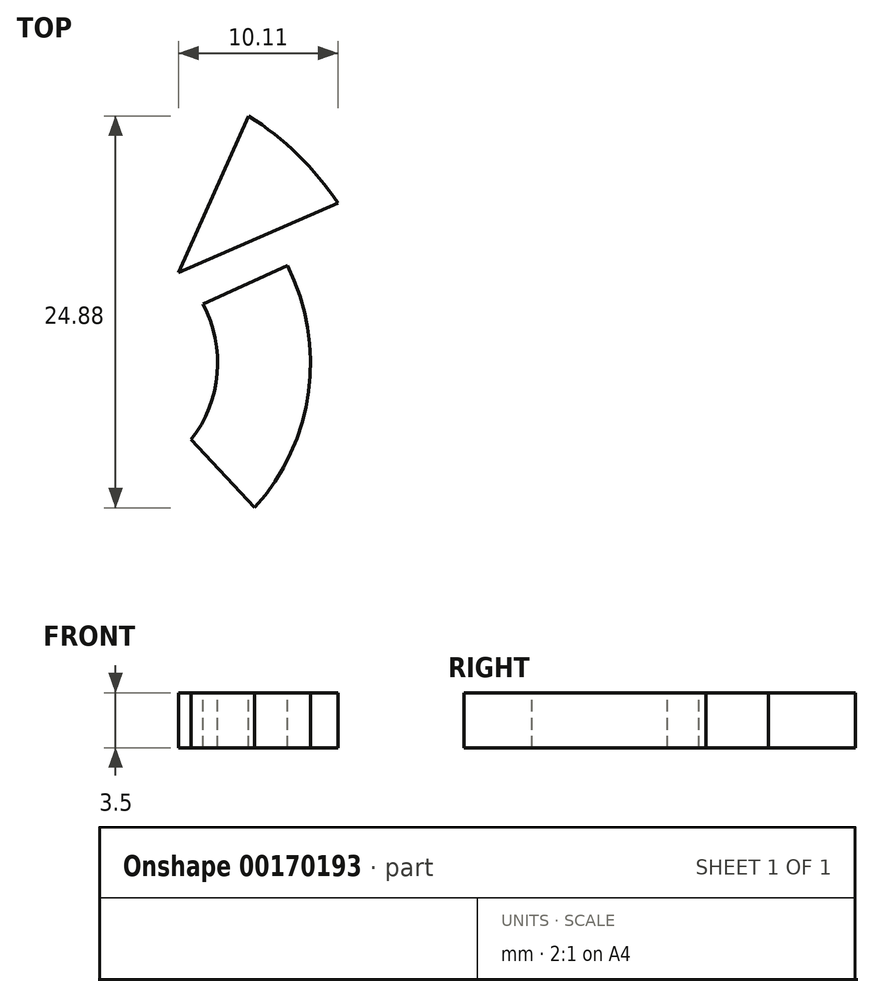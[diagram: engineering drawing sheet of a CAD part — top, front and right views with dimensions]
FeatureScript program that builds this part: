
annotation { "Feature Type Name" : "Feature", "Feature Type Description" : "" }
export const myFeature = defineFeature(function(context is Context, id is Id, definition is map)
    precondition{}
    {
        {
            var Q0;
            Q0=qCreatedBy(makeId("Top.planeOp"),FACE);
            var sketch = newSketch(context, id + "F0", { "sketchPlane" : qUnion([Q0])});
            skLineSegment(sketch, "E0.bottom", {"start": v(-153.76, 79.26) * mm, "end": v(196.24, 79.26) * mm});
            skLineSegment(sketch, "E0.top", {"start": v(-153.76, -13.12) * mm, "end": v(196.24, -13.12) * mm});
            skLineSegment(sketch, "E0.left", {"start": v(-153.76, 79.26) * mm, "end": v(-153.76, -13.12) * mm});
            skLineSegment(sketch, "E0.right", {"start": v(196.24, 79.26) * mm, "end": v(196.24, -13.12) * mm});
            skCircle(sketch, "E1", {"center": v(-123.39, 12.33) * mm, "radius": 17.49 * mm});
            skCircle(sketch, "E2", {"center": v(-123.39, 12.33) * mm, "radius": 11.88 * mm});
            skCircle(sketch, "E3", {"center": v(-123.39, 12.33) * mm, "radius": 9.49 * mm});
            skCircle(sketch, "E4", {"center": v(-123.39, 12.33) * mm, "radius": 3.6 * mm});
            skCircle(sketch, "E5", {"center": v(-123.39, 12.33) * mm, "radius": 7.83 * mm});
            skCircle(sketch, "E6", {"center": v(-123.39, 12.33) * mm, "radius": 13.72 * mm});
            skLineSegment(sketch, "E7", {"start": v(-123.39, 12.33) * mm, "end": v(-116.12, 28.24) * mm});
            skLineSegment(sketch, "E8", {"start": v(-112.54, -1.39) * mm, "end": v(-121.72, 9.15) * mm});
            skCircle(sketch, "E9", {"center": v(-123.39, 12.33) * mm, "radius": 18.48 * mm});
            skLineSegment(sketch, "E10", {"start": v(-118.04, 18.06) * mm, "end": v(-113.59, 28) * mm});
            skLineSegment(sketch, "E11", {"start": v(-118.04, 18.06) * mm, "end": v(-107.93, 22.47) * mm});
            skLineSegment(sketch, "E12", {"start": v(-116.5, 16.06) * mm, "end": v(-111.14, 18.51) * mm});
            skLineSegment(sketch, "E13", {"start": v(-117.25, 7.47) * mm, "end": v(-113.21, 3.13) * mm});
            skText(sketch, "E14", { "text": "Ecoles Supérieures", "fontName": "OpenSans-Regular.ttf"});
            skText(sketch, "E15", { "text": "CCI PORTES DE NORMANDIE", "fontName": "OpenSans-Regular.ttf"});
            const initialGuessF0  = {"E14": [-0.14265, 0.03824, 1, 0, 0.02692], "E15": [-0.10308, 0.00715, 1, 0, 0.01356]};
            skSetInitialGuess(sketch, initialGuessF0);
            skSolve(sketch);
        }
        {
            var Q0;
            Q0=makeQuery(id+"F0.imprint","IMPRINT",FACE,{"disambiguationData":[TD([[makeQuery(id+"F0.imprint","IMPRINT",EDGE,{"derivedFrom":sQuery(id+"F0.wireOp",EDGE,"E14.sketch_text.stroke-0")}),-1.0]])]});
            var Q1;
            Q1=makeQuery(id+"F0.imprint","IMPRINT",FACE,{"disambiguationData":[TD([[makeQuery(id+"F0.imprint","IMPRINT",EDGE,{"derivedFrom":sQuery(id+"F0.wireOp",EDGE,"E14.sketch_text.stroke-12")}),-1.0]])]});
            var Q2;
            Q2=makeQuery(id+"F0.imprint","IMPRINT",FACE,{"disambiguationData":[TD([[makeQuery(id+"F0.imprint","IMPRINT",EDGE,{"derivedFrom":sQuery(id+"F0.wireOp",EDGE,"E14.sketch_text.stroke-27")}),-1.0]])]});
            var Q3;
            Q3=makeQuery(id+"F0.imprint","IMPRINT",FACE,{"disambiguationData":[TD([[makeQuery(id+"F0.imprint","IMPRINT",EDGE,{"derivedFrom":sQuery(id+"F0.wireOp",EDGE,"E14.sketch_text.stroke-44")}),-1.0]])]});
            var Q4;
            Q4=makeQuery(id+"F0.imprint","IMPRINT",FACE,{"disambiguationData":[TD([[makeQuery(id+"F0.imprint","IMPRINT",EDGE,{"derivedFrom":sQuery(id+"F0.wireOp",EDGE,"E14.sketch_text.stroke-48")}),-1.0]])]});
            var Q5;
            Q5=makeQuery(id+"F0.imprint","IMPRINT",FACE,{"disambiguationData":[TD([[makeQuery(id+"F0.imprint","IMPRINT",EDGE,{"derivedFrom":sQuery(id+"F0.wireOp",EDGE,"E14.sketch_text.stroke-67")}),-1.0]])]});
            var Q6;
            Q6=makeQuery(id+"F0.imprint","IMPRINT",FACE,{"disambiguationData":[TD([[makeQuery(id+"F0.imprint","IMPRINT",EDGE,{"derivedFrom":sQuery(id+"F0.wireOp",EDGE,"E14.sketch_text.stroke-92")}),-1.0]])]});
            var Q7;
            Q7=makeQuery(id+"F0.imprint","IMPRINT",FACE,{"disambiguationData":[TD([[makeQuery(id+"F0.imprint","IMPRINT",EDGE,{"derivedFrom":sQuery(id+"F0.wireOp",EDGE,"E14.sketch_text.stroke-117")}),-1.0]])]});
            var Q8;
            Q8=makeQuery(id+"F0.imprint","IMPRINT",FACE,{"disambiguationData":[TD([[makeQuery(id+"F0.imprint","IMPRINT",EDGE,{"derivedFrom":sQuery(id+"F0.wireOp",EDGE,"E14.sketch_text.stroke-134")}),-1.0]])]});
            var Q9;
            Q9=makeQuery(id+"F0.imprint","IMPRINT",FACE,{"disambiguationData":[TD([[makeQuery(id+"F0.imprint","IMPRINT",EDGE,{"derivedFrom":sQuery(id+"F0.wireOp",EDGE,"E15.sketch_text.stroke-34")}),-1.0]])]});
            var Q10;
            Q10=makeQuery(id+"F0.imprint","IMPRINT",FACE,{"disambiguationData":[TD([[makeQuery(id+"F0.imprint","IMPRINT",EDGE,{"derivedFrom":sQuery(id+"F0.wireOp",EDGE,"E15.sketch_text.stroke-49")}),-1.0]])]});
            var Q11;
            Q11=makeQuery(id+"F0.imprint","IMPRINT",FACE,{"disambiguationData":[TD([[makeQuery(id+"F0.imprint","IMPRINT",EDGE,{"derivedFrom":sQuery(id+"F0.wireOp",EDGE,"E15.sketch_text.stroke-65")}),-1.0]])]});
            var Q12;
            Q12=makeQuery(id+"F0.imprint","IMPRINT",FACE,{"disambiguationData":[TD([[makeQuery(id+"F0.imprint","IMPRINT",EDGE,{"derivedFrom":sQuery(id+"F0.wireOp",EDGE,"E15.sketch_text.stroke-83")}),-1.0]])]});
            var Q13;
            Q13=makeQuery(id+"F0.imprint","IMPRINT",FACE,{"disambiguationData":[TD([[makeQuery(id+"F0.imprint","IMPRINT",EDGE,{"derivedFrom":sQuery(id+"F0.wireOp",EDGE,"E15.sketch_text.stroke-91")}),-1.0]])]});
            var Q14;
            Q14=makeQuery(id+"F0.imprint","IMPRINT",FACE,{"disambiguationData":[TD([[makeQuery(id+"F0.imprint","IMPRINT",EDGE,{"derivedFrom":sQuery(id+"F0.wireOp",EDGE,"E15.sketch_text.stroke-0")}),-1.0]])]});
            var Q15;
            Q15=makeQuery(id+"F0.imprint","IMPRINT",FACE,{"disambiguationData":[TD([[makeQuery(id+"F0.imprint","IMPRINT",EDGE,{"derivedFrom":sQuery(id+"F0.wireOp",EDGE,"E15.sketch_text.stroke-15")}),-1.0]])]});
            var Q16;
            Q16=makeQuery(id+"F0.imprint","IMPRINT",FACE,{"disambiguationData":[TD([[makeQuery(id+"F0.imprint","IMPRINT",EDGE,{"derivedFrom":sQuery(id+"F0.wireOp",EDGE,"E15.sketch_text.stroke-30")}),-1.0]])]});
            var Q17;
            Q17=makeQuery(id+"F0.imprint","IMPRINT",FACE,{"disambiguationData":[TD([[makeQuery(id+"F0.imprint","IMPRINT",EDGE,{"derivedFrom":sQuery(id+"F0.wireOp",EDGE,"E14.sketch_text.stroke-159")}),-1.0]])]});
            var Q18;
            Q18=makeQuery(id+"F0.imprint","IMPRINT",FACE,{"disambiguationData":[TD([[makeQuery(id+"F0.imprint","IMPRINT",EDGE,{"derivedFrom":sQuery(id+"F0.wireOp",EDGE,"E14.sketch_text.stroke-178")}),-1.0]])]});
            var Q19;
            Q19=makeQuery(id+"F0.imprint","IMPRINT",FACE,{"disambiguationData":[TD([[makeQuery(id+"F0.imprint","IMPRINT",EDGE,{"derivedFrom":sQuery(id+"F0.wireOp",EDGE,"E14.sketch_text.stroke-186")}),-1.0]])]});
            var Q20;
            Q20=makeQuery(id+"F0.imprint","IMPRINT",FACE,{"disambiguationData":[TD([[makeQuery(id+"F0.imprint","IMPRINT",EDGE,{"derivedFrom":sQuery(id+"F0.wireOp",EDGE,"E14.sketch_text.stroke-230")}),-1.0]])]});
            var Q21;
            Q21=makeQuery(id+"F0.imprint","IMPRINT",FACE,{"disambiguationData":[TD([[makeQuery(id+"F0.imprint","IMPRINT",EDGE,{"derivedFrom":sQuery(id+"F0.wireOp",EDGE,"E14.sketch_text.stroke-247")}),-1.0]])]});
            var Q22;
            Q22=makeQuery(id+"F0.imprint","IMPRINT",FACE,{"disambiguationData":[TD([[makeQuery(id+"F0.imprint","IMPRINT",EDGE,{"derivedFrom":sQuery(id+"F0.wireOp",EDGE,"E14.sketch_text.stroke-279")}),-1.0]])]});
            var Q23;
            Q23=makeQuery(id+"F0.imprint","IMPRINT",FACE,{"disambiguationData":[TD([[makeQuery(id+"F0.imprint","IMPRINT",EDGE,{"derivedFrom":sQuery(id+"F0.wireOp",EDGE,"E14.sketch_text.stroke-260")}),-1.0]])]});
            var Q24;
            Q24=makeQuery(id+"F0.imprint","IMPRINT",FACE,{"disambiguationData":[TD([[makeQuery(id+"F0.imprint","IMPRINT",EDGE,{"derivedFrom":sQuery(id+"F0.wireOp",EDGE,"E14.sketch_text.stroke-211")}),-1.0]])]});
            var Q25;
            Q25=makeQuery(id+"F0.imprint","IMPRINT",FACE,{"disambiguationData":[TD([[makeQuery(id+"F0.imprint","IMPRINT",EDGE,{"derivedFrom":sQuery(id+"F0.wireOp",EDGE,"E14.sketch_text.stroke-199")}),-1.0]])]});
            var Q26;
            Q26=makeQuery(id+"F0.imprint","IMPRINT",FACE,{"disambiguationData":[TD([[makeQuery(id+"F0.imprint","IMPRINT",EDGE,{"derivedFrom":sQuery(id+"F0.wireOp",EDGE,"E14.sketch_text.stroke-203")}),-1.0]])]});
            var Q27;
            Q27=makeQuery(id+"F0.imprint","IMPRINT",FACE,{"disambiguationData":[TD([[makeQuery(id+"F0.imprint","IMPRINT",EDGE,{"derivedFrom":sQuery(id+"F0.wireOp",EDGE,"E15.sketch_text.stroke-263")}),-1.0]])]});
            var Q28;
            Q28=makeQuery(id+"F0.imprint","IMPRINT",FACE,{"disambiguationData":[TD([[makeQuery(id+"F0.imprint","IMPRINT",EDGE,{"derivedFrom":sQuery(id+"F0.wireOp",EDGE,"E15.sketch_text.stroke-267")}),-1.0]])]});
            var Q29;
            Q29=makeQuery(id+"F0.imprint","IMPRINT",FACE,{"disambiguationData":[TD([[makeQuery(id+"F0.imprint","IMPRINT",EDGE,{"derivedFrom":sQuery(id+"F0.wireOp",EDGE,"E15.sketch_text.stroke-249")}),-1.0]])]});
            var Q30;
            Q30=makeQuery(id+"F0.imprint","IMPRINT",FACE,{"disambiguationData":[TD([[makeQuery(id+"F0.imprint","IMPRINT",EDGE,{"derivedFrom":sQuery(id+"F0.wireOp",EDGE,"E15.sketch_text.stroke-103")}),-1.0]])]});
            var Q31;
            Q31=makeQuery(id+"F0.imprint","IMPRINT",FACE,{"disambiguationData":[TD([[makeQuery(id+"F0.imprint","IMPRINT",EDGE,{"derivedFrom":sQuery(id+"F0.wireOp",EDGE,"E15.sketch_text.stroke-128")}),-1.0]])]});
            var Q32;
            Q32=makeQuery(id+"F0.imprint","IMPRINT",FACE,{"disambiguationData":[TD([[makeQuery(id+"F0.imprint","IMPRINT",EDGE,{"derivedFrom":sQuery(id+"F0.wireOp",EDGE,"E15.sketch_text.stroke-154")}),-1.0]])]});
            var Q33;
            Q33=makeQuery(id+"F0.imprint","IMPRINT",FACE,{"disambiguationData":[TD([[makeQuery(id+"F0.imprint","IMPRINT",EDGE,{"derivedFrom":sQuery(id+"F0.wireOp",EDGE,"E15.sketch_text.stroke-142")}),-1.0]])]});
            var Q34;
            Q34=makeQuery(id+"F0.imprint","IMPRINT",FACE,{"disambiguationData":[TD([[makeQuery(id+"F0.imprint","IMPRINT",EDGE,{"derivedFrom":sQuery(id+"F0.wireOp",EDGE,"E15.sketch_text.stroke-169")}),-1.0]])]});
            var Q35;
            Q35=makeQuery(id+"F0.imprint","IMPRINT",FACE,{"disambiguationData":[TD([[makeQuery(id+"F0.imprint","IMPRINT",EDGE,{"derivedFrom":sQuery(id+"F0.wireOp",EDGE,"E15.sketch_text.stroke-185")}),-1.0]])]});
            var Q36;
            Q36=makeQuery(id+"F0.imprint","IMPRINT",FACE,{"disambiguationData":[TD([[makeQuery(id+"F0.imprint","IMPRINT",EDGE,{"derivedFrom":sQuery(id+"F0.wireOp",EDGE,"E15.sketch_text.stroke-203")}),-1.0]])]});
            var Q37;
            Q37=makeQuery(id+"F0.imprint","IMPRINT",FACE,{"disambiguationData":[TD([[makeQuery(id+"F0.imprint","IMPRINT",EDGE,{"derivedFrom":sQuery(id+"F0.wireOp",EDGE,"E15.sketch_text.stroke-234")}),-1.0]])]});
            var Q38;
            Q38=makeQuery(id+"F0.imprint","IMPRINT",FACE,{"disambiguationData":[TD([[makeQuery(id+"F0.imprint","IMPRINT",EDGE,{"derivedFrom":sQuery(id+"F0.wireOp",EDGE,"E15.sketch_text.stroke-221")}),-1.0]])]});
            var Q39;
            {var subQ0=sQuery(id+"F0.wireOp",EDGE,"E8");var subQ1=sQuery(id+"F0.wireOp",EDGE,"E4");var subQ2=makeQuery(id+"F0.imprint","INTERSECT",VERTEX,{"derivedFrom":[subQ1,subQ0]});Q39=makeQuery(id+"F0.imprint","IMPRINT",FACE,{"disambiguationData":[TD([[makeQuery(id+"F0.imprint","IMPRINT",EDGE,{"disambiguationData":[TD([[subQ2,1.0]])],"derivedFrom":subQ1}),-1.0]])]});}
            var Q40;
            {var subQ0=sQuery(id+"F0.wireOp",EDGE,"E7");var subQ1=sQuery(id+"F0.wireOp",EDGE,"E3");var subQ2=makeQuery(id+"F0.imprint","INTERSECT",VERTEX,{"derivedFrom":[subQ1,subQ0]});Q40=makeQuery(id+"F0.imprint","IMPRINT",FACE,{"disambiguationData":[TD([[makeQuery(id+"F0.imprint","IMPRINT",EDGE,{"disambiguationData":[TD([[subQ2,-1.0]])],"derivedFrom":subQ1}),1.0]])]});}
            var Q41;
            {var subQ0=sQuery(id+"F0.wireOp",EDGE,"E7");var subQ1=sQuery(id+"F0.wireOp",EDGE,"E2");var subQ2=makeQuery(id+"F0.imprint","INTERSECT",VERTEX,{"derivedFrom":[subQ1,subQ0]});Q41=makeQuery(id+"F0.imprint","IMPRINT",FACE,{"disambiguationData":[TD([[makeQuery(id+"F0.imprint","IMPRINT",EDGE,{"disambiguationData":[TD([[subQ2,-1.0]])],"derivedFrom":subQ1}),-1.0]])]});}
            var Q42;
            {var subQ0=sQuery(id+"F0.wireOp",EDGE,"E7");var subQ1=sQuery(id+"F0.wireOp",EDGE,"E1");var subQ2=makeQuery(id+"F0.imprint","INTERSECT",VERTEX,{"derivedFrom":[subQ1,subQ0]});Q42=makeQuery(id+"F0.imprint","IMPRINT",FACE,{"disambiguationData":[TD([[makeQuery(id+"F0.imprint","IMPRINT",EDGE,{"disambiguationData":[TD([[subQ2,-1.0]])],"derivedFrom":subQ1}),1.0]])]});}
            extrude(context, id + "F1", {"entities" : qUnion([Q0, Q1, Q2, Q3, Q4, Q5, Q6, Q7, Q8, Q9, Q10, Q11, Q12, Q13, Q14, Q15, Q16, Q17, Q18, Q19, Q20, Q21, Q22, Q23, Q24, Q25, Q26, Q27, Q28, Q29, Q30, Q31, Q32, Q33, Q34, Q35, Q36, Q37, Q38, Q39, Q40, Q41, Q42]), "depth" : 1.5 * mm});
        }
        {
            var Q0;
            Q0=makeQuery(id+"F0.imprint","IMPRINT",FACE,{"disambiguationData":[TD([[makeQuery(id+"F0.imprint","IMPRINT",EDGE,{"derivedFrom":sQuery(id+"F0.wireOp",EDGE,"E0.bottom")}),-1.0]])]});
            var sketch = newSketch(context, id + "F2", { "sketchPlane" : qUnion([Q0])});
            skLineSegment(sketch, "E16.bottom", {"start": v(-154.27, -13.4) * mm, "end": v(196.36, -13.4) * mm});
            skLineSegment(sketch, "E16.top", {"start": v(-154.27, 78.37) * mm, "end": v(196.36, 78.37) * mm});
            skLineSegment(sketch, "E16.left", {"start": v(-154.27, -13.4) * mm, "end": v(-154.27, 78.37) * mm});
            skLineSegment(sketch, "E16.right", {"start": v(196.36, -13.4) * mm, "end": v(196.36, 78.37) * mm});
            skSolve(sketch);
        }
        {
            var Q0;
            Q0=qSketchRegion(id+"F2",true);
            var Q1;
            {var subQ5=makeQuery(id+"F0.imprint","IMPRINT",EDGE,{"derivedFrom":sQuery(id+"F0.wireOp",EDGE,"E0.top")});Q1=makeQuery(id+"F2.imprint","IMPRINT",FACE,{"disambiguationData":[TD([[makeQuery(id+"F2.imprint","IMPRINT",EDGE,{"derivedFrom":subQ5}),1.0]])]});}
            extrude(context, id + "F3", {"entities" : qUnion([Q0, Q1]), "oppositeDirection" : true, "depth" : 2.7 * mm});
        }
        {
            var Q0;
            Q0=makeQuery(id+"F3.opExtrude","SWEPT_EDGE",EDGE,{"disambiguationData":[OSD([sQuery(id+"F2.wireOp",EDGE,"E16.bottom"),sQuery(id+"F2.wireOp",EDGE,"E16.right")])]});
            var Q1;
            Q1=makeQuery(id+"F3.opExtrude","SWEPT_EDGE",EDGE,{"disambiguationData":[OSD([sQuery(id+"F2.wireOp",EDGE,"E16.top"),sQuery(id+"F2.wireOp",EDGE,"E16.right")])]});
            var Q2;
            Q2=makeQuery(id+"F3.opExtrude","SWEPT_EDGE",EDGE,{"disambiguationData":[OSD([sQuery(id+"F2.wireOp",EDGE,"E16.bottom"),sQuery(id+"F2.wireOp",EDGE,"E16.left")])]});
            var Q3;
            Q3=makeQuery(id+"F3.opExtrude","SWEPT_EDGE",EDGE,{"disambiguationData":[OSD([sQuery(id+"F2.wireOp",EDGE,"E16.top"),sQuery(id+"F2.wireOp",EDGE,"E16.left")])]});
            fillet(context, id + "F4", {"entities" : qUnion([Q0, Q1, Q2, Q3]), "radius" : 10 * mm, "tangentPropagation" : true, "allowEdgeOverflow" : false});
        }
        {
            var Q0;
            {var subQ0=sQuery(id+"F0.wireOp",EDGE,"E12");var subQ1=sQuery(id+"F0.wireOp",EDGE,"E3");var subQ2=makeQuery(id+"F0.imprint","INTERSECT",VERTEX,{"derivedFrom":[subQ1,subQ0]});Q0=makeQuery(id+"F0.imprint","IMPRINT",FACE,{"disambiguationData":[TD([[makeQuery(id+"F0.imprint","IMPRINT",EDGE,{"disambiguationData":[TD([[subQ2,1.0]])],"derivedFrom":subQ1}),1.0]])]});}
            var Q1;
            {var subQ0=sQuery(id+"F0.wireOp",EDGE,"E12");var subQ1=sQuery(id+"F0.wireOp",EDGE,"E2");var subQ2=makeQuery(id+"F0.imprint","INTERSECT",VERTEX,{"derivedFrom":[subQ1,subQ0]});Q1=makeQuery(id+"F0.imprint","IMPRINT",FACE,{"disambiguationData":[TD([[makeQuery(id+"F0.imprint","IMPRINT",EDGE,{"disambiguationData":[TD([[subQ2,1.0]])],"derivedFrom":subQ1}),1.0]])]});}
            var Q2;
            {var subQ0=sQuery(id+"F0.wireOp",EDGE,"E12");var subQ1=sQuery(id+"F0.wireOp",EDGE,"E2");var subQ2=makeQuery(id+"F0.imprint","INTERSECT",VERTEX,{"derivedFrom":[subQ1,subQ0]});Q2=makeQuery(id+"F0.imprint","IMPRINT",FACE,{"disambiguationData":[TD([[makeQuery(id+"F0.imprint","IMPRINT",EDGE,{"disambiguationData":[TD([[subQ2,1.0]])],"derivedFrom":subQ1}),-1.0]])]});}
            var Q3;
            {var subQ0=sQuery(id+"F0.wireOp",EDGE,"E11");var subQ1=sQuery(id+"F0.wireOp",EDGE,"E3");var subQ2=makeQuery(id+"F0.imprint","INTERSECT",VERTEX,{"derivedFrom":[subQ1,subQ0]});Q3=makeQuery(id+"F0.imprint","IMPRINT",FACE,{"disambiguationData":[TD([[makeQuery(id+"F0.imprint","IMPRINT",EDGE,{"disambiguationData":[TD([[subQ2,-1.0]])],"derivedFrom":subQ1}),1.0]])]});}
            var Q4;
            {var subQ0=sQuery(id+"F0.wireOp",EDGE,"E11");var subQ1=sQuery(id+"F0.wireOp",EDGE,"E2");var subQ2=makeQuery(id+"F0.imprint","INTERSECT",VERTEX,{"derivedFrom":[subQ1,subQ0]});Q4=makeQuery(id+"F0.imprint","IMPRINT",FACE,{"disambiguationData":[TD([[makeQuery(id+"F0.imprint","IMPRINT",EDGE,{"disambiguationData":[TD([[subQ2,-1.0]])],"derivedFrom":subQ1}),1.0]])]});}
            var Q5;
            {var subQ0=sQuery(id+"F0.wireOp",EDGE,"E10");var subQ1=sQuery(id+"F0.wireOp",EDGE,"E1");var subQ2=makeQuery(id+"F0.imprint","INTERSECT",VERTEX,{"derivedFrom":[subQ1,subQ0]});Q5=makeQuery(id+"F0.imprint","IMPRINT",FACE,{"disambiguationData":[TD([[makeQuery(id+"F0.imprint","IMPRINT",EDGE,{"disambiguationData":[TD([[subQ2,1.0]])],"derivedFrom":subQ1}),1.0]])]});}
            var Q6;
            {var subQ0=sQuery(id+"F0.wireOp",EDGE,"E10");var subQ1=sQuery(id+"F0.wireOp",EDGE,"E1");var subQ2=makeQuery(id+"F0.imprint","INTERSECT",VERTEX,{"derivedFrom":[subQ1,subQ0]});Q6=makeQuery(id+"F0.imprint","IMPRINT",FACE,{"disambiguationData":[TD([[makeQuery(id+"F0.imprint","IMPRINT",EDGE,{"disambiguationData":[TD([[subQ2,1.0]])],"derivedFrom":subQ1}),-1.0]])]});}
            var Q7;
            {var subQ0=sQuery(id+"F0.wireOp",EDGE,"E11");var subQ1=sQuery(id+"F0.wireOp",EDGE,"E2");var subQ2=makeQuery(id+"F0.imprint","INTERSECT",VERTEX,{"derivedFrom":[subQ1,subQ0]});Q7=makeQuery(id+"F0.imprint","IMPRINT",FACE,{"disambiguationData":[TD([[makeQuery(id+"F0.imprint","IMPRINT",EDGE,{"disambiguationData":[TD([[subQ2,-1.0]])],"derivedFrom":subQ1}),-1.0]])]});}
            extrude(context, id + "F5", {"entities" : qUnion([Q0, Q1, Q2, Q3, Q4, Q5, Q6, Q7]), "oppositeDirection" : true, "depth" : 2 * mm, "hasSecondDirection" : true, "secondDirectionOppositeDirection" : false, "secondDirectionDepth" : 1.5 * mm});
        }
        {
            var Q0;
            Q0=makeQuery(id+"F1.opExtrude","SWEPT_BODY",BODY,{"disambiguationData":[OSD([sQuery(id+"F0.wireOp",EDGE,"E1"),sQuery(id+"F0.wireOp",EDGE,"E2"),sQuery(id+"F0.wireOp",EDGE,"E7"),sQuery(id+"F0.wireOp",EDGE,"E8")])]});
            var Q1;
            Q1=makeQuery(id+"F1.opExtrude","SWEPT_BODY",BODY,{"disambiguationData":[OSD([sQuery(id+"F0.wireOp",EDGE,"E3"),sQuery(id+"F0.wireOp",EDGE,"E4"),sQuery(id+"F0.wireOp",EDGE,"E7"),sQuery(id+"F0.wireOp",EDGE,"E8")])]});
            var Q2;
            Q2=makeQuery(id+"F1.opExtrude","SWEPT_BODY",BODY,{"disambiguationData":[OSD([sQuery(id+"F0.wireOp",EDGE,"E14.sketch_text.stroke-0"),sQuery(id+"F0.wireOp",EDGE,"E14.sketch_text.stroke-1"),sQuery(id+"F0.wireOp",EDGE,"E14.sketch_text.stroke-2"),sQuery(id+"F0.wireOp",EDGE,"E14.sketch_text.stroke-3"),sQuery(id+"F0.wireOp",EDGE,"E14.sketch_text.stroke-4"),sQuery(id+"F0.wireOp",EDGE,"E14.sketch_text.stroke-5"),sQuery(id+"F0.wireOp",EDGE,"E14.sketch_text.stroke-6"),sQuery(id+"F0.wireOp",EDGE,"E14.sketch_text.stroke-7"),sQuery(id+"F0.wireOp",EDGE,"E14.sketch_text.stroke-8"),sQuery(id+"F0.wireOp",EDGE,"E14.sketch_text.stroke-9"),sQuery(id+"F0.wireOp",EDGE,"E14.sketch_text.stroke-10"),sQuery(id+"F0.wireOp",EDGE,"E14.sketch_text.stroke-11")])]});
            var Q3;
            Q3=makeQuery(id+"F1.opExtrude","SWEPT_BODY",BODY,{"disambiguationData":[OSD([sQuery(id+"F0.wireOp",EDGE,"E14.sketch_text.stroke-12"),sQuery(id+"F0.wireOp",EDGE,"E14.sketch_text.stroke-13"),sQuery(id+"F0.wireOp",EDGE,"E14.sketch_text.stroke-14"),sQuery(id+"F0.wireOp",EDGE,"E14.sketch_text.stroke-15"),sQuery(id+"F0.wireOp",EDGE,"E14.sketch_text.stroke-16"),sQuery(id+"F0.wireOp",EDGE,"E14.sketch_text.stroke-17"),sQuery(id+"F0.wireOp",EDGE,"E14.sketch_text.stroke-18"),sQuery(id+"F0.wireOp",EDGE,"E14.sketch_text.stroke-19"),sQuery(id+"F0.wireOp",EDGE,"E14.sketch_text.stroke-20"),sQuery(id+"F0.wireOp",EDGE,"E14.sketch_text.stroke-21"),sQuery(id+"F0.wireOp",EDGE,"E14.sketch_text.stroke-22"),sQuery(id+"F0.wireOp",EDGE,"E14.sketch_text.stroke-23"),sQuery(id+"F0.wireOp",EDGE,"E14.sketch_text.stroke-24"),sQuery(id+"F0.wireOp",EDGE,"E14.sketch_text.stroke-25"),sQuery(id+"F0.wireOp",EDGE,"E14.sketch_text.stroke-26")])]});
            var Q4;
            Q4=makeQuery(id+"F1.opExtrude","SWEPT_BODY",BODY,{"disambiguationData":[OSD([sQuery(id+"F0.wireOp",EDGE,"E14.sketch_text.stroke-27"),sQuery(id+"F0.wireOp",EDGE,"E14.sketch_text.stroke-28"),sQuery(id+"F0.wireOp",EDGE,"E14.sketch_text.stroke-29"),sQuery(id+"F0.wireOp",EDGE,"E14.sketch_text.stroke-30"),sQuery(id+"F0.wireOp",EDGE,"E14.sketch_text.stroke-31"),sQuery(id+"F0.wireOp",EDGE,"E14.sketch_text.stroke-32"),sQuery(id+"F0.wireOp",EDGE,"E14.sketch_text.stroke-33"),sQuery(id+"F0.wireOp",EDGE,"E14.sketch_text.stroke-34"),sQuery(id+"F0.wireOp",EDGE,"E14.sketch_text.stroke-35"),sQuery(id+"F0.wireOp",EDGE,"E14.sketch_text.stroke-36"),sQuery(id+"F0.wireOp",EDGE,"E14.sketch_text.stroke-37"),sQuery(id+"F0.wireOp",EDGE,"E14.sketch_text.stroke-38"),sQuery(id+"F0.wireOp",EDGE,"E14.sketch_text.stroke-39"),sQuery(id+"F0.wireOp",EDGE,"E14.sketch_text.stroke-40"),sQuery(id+"F0.wireOp",EDGE,"E14.sketch_text.stroke-41"),sQuery(id+"F0.wireOp",EDGE,"E14.sketch_text.stroke-42"),sQuery(id+"F0.wireOp",EDGE,"E14.sketch_text.stroke-43")])]});
            var Q5;
            Q5=makeQuery(id+"F1.opExtrude","SWEPT_BODY",BODY,{"disambiguationData":[OSD([sQuery(id+"F0.wireOp",EDGE,"E14.sketch_text.stroke-44"),sQuery(id+"F0.wireOp",EDGE,"E14.sketch_text.stroke-45"),sQuery(id+"F0.wireOp",EDGE,"E14.sketch_text.stroke-46"),sQuery(id+"F0.wireOp",EDGE,"E14.sketch_text.stroke-47")])]});
            var Q6;
            Q6=makeQuery(id+"F1.opExtrude","SWEPT_BODY",BODY,{"disambiguationData":[OSD([sQuery(id+"F0.wireOp",EDGE,"E14.sketch_text.stroke-48"),sQuery(id+"F0.wireOp",EDGE,"E14.sketch_text.stroke-49"),sQuery(id+"F0.wireOp",EDGE,"E14.sketch_text.stroke-50"),sQuery(id+"F0.wireOp",EDGE,"E14.sketch_text.stroke-51"),sQuery(id+"F0.wireOp",EDGE,"E14.sketch_text.stroke-52"),sQuery(id+"F0.wireOp",EDGE,"E14.sketch_text.stroke-53"),sQuery(id+"F0.wireOp",EDGE,"E14.sketch_text.stroke-54"),sQuery(id+"F0.wireOp",EDGE,"E14.sketch_text.stroke-55"),sQuery(id+"F0.wireOp",EDGE,"E14.sketch_text.stroke-56"),sQuery(id+"F0.wireOp",EDGE,"E14.sketch_text.stroke-57"),sQuery(id+"F0.wireOp",EDGE,"E14.sketch_text.stroke-58"),sQuery(id+"F0.wireOp",EDGE,"E14.sketch_text.stroke-59"),sQuery(id+"F0.wireOp",EDGE,"E14.sketch_text.stroke-60"),sQuery(id+"F0.wireOp",EDGE,"E14.sketch_text.stroke-61"),sQuery(id+"F0.wireOp",EDGE,"E14.sketch_text.stroke-62"),sQuery(id+"F0.wireOp",EDGE,"E14.sketch_text.stroke-63"),sQuery(id+"F0.wireOp",EDGE,"E14.sketch_text.stroke-64"),sQuery(id+"F0.wireOp",EDGE,"E14.sketch_text.stroke-65"),sQuery(id+"F0.wireOp",EDGE,"E14.sketch_text.stroke-66")])]});
            var Q7;
            Q7=makeQuery(id+"F1.opExtrude","SWEPT_BODY",BODY,{"disambiguationData":[OSD([sQuery(id+"F0.wireOp",EDGE,"E14.sketch_text.stroke-67"),sQuery(id+"F0.wireOp",EDGE,"E14.sketch_text.stroke-68"),sQuery(id+"F0.wireOp",EDGE,"E14.sketch_text.stroke-69"),sQuery(id+"F0.wireOp",EDGE,"E14.sketch_text.stroke-70"),sQuery(id+"F0.wireOp",EDGE,"E14.sketch_text.stroke-71"),sQuery(id+"F0.wireOp",EDGE,"E14.sketch_text.stroke-72"),sQuery(id+"F0.wireOp",EDGE,"E14.sketch_text.stroke-73"),sQuery(id+"F0.wireOp",EDGE,"E14.sketch_text.stroke-74"),sQuery(id+"F0.wireOp",EDGE,"E14.sketch_text.stroke-75"),sQuery(id+"F0.wireOp",EDGE,"E14.sketch_text.stroke-76"),sQuery(id+"F0.wireOp",EDGE,"E14.sketch_text.stroke-77"),sQuery(id+"F0.wireOp",EDGE,"E14.sketch_text.stroke-78"),sQuery(id+"F0.wireOp",EDGE,"E14.sketch_text.stroke-79"),sQuery(id+"F0.wireOp",EDGE,"E14.sketch_text.stroke-80"),sQuery(id+"F0.wireOp",EDGE,"E14.sketch_text.stroke-81"),sQuery(id+"F0.wireOp",EDGE,"E14.sketch_text.stroke-82"),sQuery(id+"F0.wireOp",EDGE,"E14.sketch_text.stroke-83"),sQuery(id+"F0.wireOp",EDGE,"E14.sketch_text.stroke-84"),sQuery(id+"F0.wireOp",EDGE,"E14.sketch_text.stroke-85"),sQuery(id+"F0.wireOp",EDGE,"E14.sketch_text.stroke-86"),sQuery(id+"F0.wireOp",EDGE,"E14.sketch_text.stroke-87"),sQuery(id+"F0.wireOp",EDGE,"E14.sketch_text.stroke-88"),sQuery(id+"F0.wireOp",EDGE,"E14.sketch_text.stroke-89"),sQuery(id+"F0.wireOp",EDGE,"E14.sketch_text.stroke-90"),sQuery(id+"F0.wireOp",EDGE,"E14.sketch_text.stroke-91")])]});
            var Q8;
            Q8=makeQuery(id+"F1.opExtrude","SWEPT_BODY",BODY,{"disambiguationData":[OSD([sQuery(id+"F0.wireOp",EDGE,"E14.sketch_text.stroke-92"),sQuery(id+"F0.wireOp",EDGE,"E14.sketch_text.stroke-93"),sQuery(id+"F0.wireOp",EDGE,"E14.sketch_text.stroke-94"),sQuery(id+"F0.wireOp",EDGE,"E14.sketch_text.stroke-95"),sQuery(id+"F0.wireOp",EDGE,"E14.sketch_text.stroke-96"),sQuery(id+"F0.wireOp",EDGE,"E14.sketch_text.stroke-97"),sQuery(id+"F0.wireOp",EDGE,"E14.sketch_text.stroke-98"),sQuery(id+"F0.wireOp",EDGE,"E14.sketch_text.stroke-99"),sQuery(id+"F0.wireOp",EDGE,"E14.sketch_text.stroke-100"),sQuery(id+"F0.wireOp",EDGE,"E14.sketch_text.stroke-101"),sQuery(id+"F0.wireOp",EDGE,"E14.sketch_text.stroke-102"),sQuery(id+"F0.wireOp",EDGE,"E14.sketch_text.stroke-103"),sQuery(id+"F0.wireOp",EDGE,"E14.sketch_text.stroke-104"),sQuery(id+"F0.wireOp",EDGE,"E14.sketch_text.stroke-105"),sQuery(id+"F0.wireOp",EDGE,"E14.sketch_text.stroke-106"),sQuery(id+"F0.wireOp",EDGE,"E14.sketch_text.stroke-107"),sQuery(id+"F0.wireOp",EDGE,"E14.sketch_text.stroke-108"),sQuery(id+"F0.wireOp",EDGE,"E14.sketch_text.stroke-109"),sQuery(id+"F0.wireOp",EDGE,"E14.sketch_text.stroke-110"),sQuery(id+"F0.wireOp",EDGE,"E14.sketch_text.stroke-111"),sQuery(id+"F0.wireOp",EDGE,"E14.sketch_text.stroke-112"),sQuery(id+"F0.wireOp",EDGE,"E14.sketch_text.stroke-113"),sQuery(id+"F0.wireOp",EDGE,"E14.sketch_text.stroke-114"),sQuery(id+"F0.wireOp",EDGE,"E14.sketch_text.stroke-115"),sQuery(id+"F0.wireOp",EDGE,"E14.sketch_text.stroke-116")])]});
            var Q9;
            Q9=makeQuery(id+"F1.opExtrude","SWEPT_BODY",BODY,{"disambiguationData":[OSD([sQuery(id+"F0.wireOp",EDGE,"E14.sketch_text.stroke-117"),sQuery(id+"F0.wireOp",EDGE,"E14.sketch_text.stroke-118"),sQuery(id+"F0.wireOp",EDGE,"E14.sketch_text.stroke-119"),sQuery(id+"F0.wireOp",EDGE,"E14.sketch_text.stroke-120"),sQuery(id+"F0.wireOp",EDGE,"E14.sketch_text.stroke-121"),sQuery(id+"F0.wireOp",EDGE,"E14.sketch_text.stroke-122"),sQuery(id+"F0.wireOp",EDGE,"E14.sketch_text.stroke-123"),sQuery(id+"F0.wireOp",EDGE,"E14.sketch_text.stroke-124"),sQuery(id+"F0.wireOp",EDGE,"E14.sketch_text.stroke-125"),sQuery(id+"F0.wireOp",EDGE,"E14.sketch_text.stroke-126"),sQuery(id+"F0.wireOp",EDGE,"E14.sketch_text.stroke-127"),sQuery(id+"F0.wireOp",EDGE,"E14.sketch_text.stroke-128"),sQuery(id+"F0.wireOp",EDGE,"E14.sketch_text.stroke-129"),sQuery(id+"F0.wireOp",EDGE,"E14.sketch_text.stroke-130"),sQuery(id+"F0.wireOp",EDGE,"E14.sketch_text.stroke-131"),sQuery(id+"F0.wireOp",EDGE,"E14.sketch_text.stroke-132"),sQuery(id+"F0.wireOp",EDGE,"E14.sketch_text.stroke-133")])]});
            var Q10;
            Q10=makeQuery(id+"F1.opExtrude","SWEPT_BODY",BODY,{"disambiguationData":[OSD([sQuery(id+"F0.wireOp",EDGE,"E14.sketch_text.stroke-134"),sQuery(id+"F0.wireOp",EDGE,"E14.sketch_text.stroke-135"),sQuery(id+"F0.wireOp",EDGE,"E14.sketch_text.stroke-136"),sQuery(id+"F0.wireOp",EDGE,"E14.sketch_text.stroke-137"),sQuery(id+"F0.wireOp",EDGE,"E14.sketch_text.stroke-138"),sQuery(id+"F0.wireOp",EDGE,"E14.sketch_text.stroke-139"),sQuery(id+"F0.wireOp",EDGE,"E14.sketch_text.stroke-140"),sQuery(id+"F0.wireOp",EDGE,"E14.sketch_text.stroke-141"),sQuery(id+"F0.wireOp",EDGE,"E14.sketch_text.stroke-142"),sQuery(id+"F0.wireOp",EDGE,"E14.sketch_text.stroke-143"),sQuery(id+"F0.wireOp",EDGE,"E14.sketch_text.stroke-144"),sQuery(id+"F0.wireOp",EDGE,"E14.sketch_text.stroke-145"),sQuery(id+"F0.wireOp",EDGE,"E14.sketch_text.stroke-146"),sQuery(id+"F0.wireOp",EDGE,"E14.sketch_text.stroke-147"),sQuery(id+"F0.wireOp",EDGE,"E14.sketch_text.stroke-148"),sQuery(id+"F0.wireOp",EDGE,"E14.sketch_text.stroke-149"),sQuery(id+"F0.wireOp",EDGE,"E14.sketch_text.stroke-150"),sQuery(id+"F0.wireOp",EDGE,"E14.sketch_text.stroke-151"),sQuery(id+"F0.wireOp",EDGE,"E14.sketch_text.stroke-152"),sQuery(id+"F0.wireOp",EDGE,"E14.sketch_text.stroke-153"),sQuery(id+"F0.wireOp",EDGE,"E14.sketch_text.stroke-154"),sQuery(id+"F0.wireOp",EDGE,"E14.sketch_text.stroke-155"),sQuery(id+"F0.wireOp",EDGE,"E14.sketch_text.stroke-156"),sQuery(id+"F0.wireOp",EDGE,"E14.sketch_text.stroke-157"),sQuery(id+"F0.wireOp",EDGE,"E14.sketch_text.stroke-158")])]});
            var Q11;
            Q11=makeQuery(id+"F1.opExtrude","SWEPT_BODY",BODY,{"disambiguationData":[OSD([sQuery(id+"F0.wireOp",EDGE,"E14.sketch_text.stroke-159"),sQuery(id+"F0.wireOp",EDGE,"E14.sketch_text.stroke-160"),sQuery(id+"F0.wireOp",EDGE,"E14.sketch_text.stroke-161"),sQuery(id+"F0.wireOp",EDGE,"E14.sketch_text.stroke-162"),sQuery(id+"F0.wireOp",EDGE,"E14.sketch_text.stroke-163"),sQuery(id+"F0.wireOp",EDGE,"E14.sketch_text.stroke-164"),sQuery(id+"F0.wireOp",EDGE,"E14.sketch_text.stroke-165"),sQuery(id+"F0.wireOp",EDGE,"E14.sketch_text.stroke-166"),sQuery(id+"F0.wireOp",EDGE,"E14.sketch_text.stroke-167"),sQuery(id+"F0.wireOp",EDGE,"E14.sketch_text.stroke-168"),sQuery(id+"F0.wireOp",EDGE,"E14.sketch_text.stroke-169"),sQuery(id+"F0.wireOp",EDGE,"E14.sketch_text.stroke-170"),sQuery(id+"F0.wireOp",EDGE,"E14.sketch_text.stroke-171"),sQuery(id+"F0.wireOp",EDGE,"E14.sketch_text.stroke-172"),sQuery(id+"F0.wireOp",EDGE,"E14.sketch_text.stroke-173"),sQuery(id+"F0.wireOp",EDGE,"E14.sketch_text.stroke-174"),sQuery(id+"F0.wireOp",EDGE,"E14.sketch_text.stroke-175"),sQuery(id+"F0.wireOp",EDGE,"E14.sketch_text.stroke-176"),sQuery(id+"F0.wireOp",EDGE,"E14.sketch_text.stroke-177")])]});
            var Q12;
            Q12=makeQuery(id+"F1.opExtrude","SWEPT_BODY",BODY,{"disambiguationData":[OSD([sQuery(id+"F0.wireOp",EDGE,"E14.sketch_text.stroke-178"),sQuery(id+"F0.wireOp",EDGE,"E14.sketch_text.stroke-179"),sQuery(id+"F0.wireOp",EDGE,"E14.sketch_text.stroke-180"),sQuery(id+"F0.wireOp",EDGE,"E14.sketch_text.stroke-181"),sQuery(id+"F0.wireOp",EDGE,"E14.sketch_text.stroke-182"),sQuery(id+"F0.wireOp",EDGE,"E14.sketch_text.stroke-183"),sQuery(id+"F0.wireOp",EDGE,"E14.sketch_text.stroke-184"),sQuery(id+"F0.wireOp",EDGE,"E14.sketch_text.stroke-185")])]});
            var Q13;
            Q13=makeQuery(id+"F1.opExtrude","SWEPT_BODY",BODY,{"disambiguationData":[OSD([sQuery(id+"F0.wireOp",EDGE,"E14.sketch_text.stroke-186"),sQuery(id+"F0.wireOp",EDGE,"E14.sketch_text.stroke-187"),sQuery(id+"F0.wireOp",EDGE,"E14.sketch_text.stroke-188"),sQuery(id+"F0.wireOp",EDGE,"E14.sketch_text.stroke-189"),sQuery(id+"F0.wireOp",EDGE,"E14.sketch_text.stroke-190"),sQuery(id+"F0.wireOp",EDGE,"E14.sketch_text.stroke-191"),sQuery(id+"F0.wireOp",EDGE,"E14.sketch_text.stroke-192"),sQuery(id+"F0.wireOp",EDGE,"E14.sketch_text.stroke-193"),sQuery(id+"F0.wireOp",EDGE,"E14.sketch_text.stroke-194"),sQuery(id+"F0.wireOp",EDGE,"E14.sketch_text.stroke-195"),sQuery(id+"F0.wireOp",EDGE,"E14.sketch_text.stroke-196"),sQuery(id+"F0.wireOp",EDGE,"E14.sketch_text.stroke-197"),sQuery(id+"F0.wireOp",EDGE,"E14.sketch_text.stroke-198")])]});
            var Q14;
            Q14=makeQuery(id+"F1.opExtrude","SWEPT_BODY",BODY,{"disambiguationData":[OSD([sQuery(id+"F0.wireOp",EDGE,"E14.sketch_text.stroke-199"),sQuery(id+"F0.wireOp",EDGE,"E14.sketch_text.stroke-200"),sQuery(id+"F0.wireOp",EDGE,"E14.sketch_text.stroke-201"),sQuery(id+"F0.wireOp",EDGE,"E14.sketch_text.stroke-202")])]});
            var Q15;
            Q15=makeQuery(id+"F1.opExtrude","SWEPT_BODY",BODY,{"disambiguationData":[OSD([sQuery(id+"F0.wireOp",EDGE,"E14.sketch_text.stroke-203"),sQuery(id+"F0.wireOp",EDGE,"E14.sketch_text.stroke-204"),sQuery(id+"F0.wireOp",EDGE,"E14.sketch_text.stroke-205"),sQuery(id+"F0.wireOp",EDGE,"E14.sketch_text.stroke-206"),sQuery(id+"F0.wireOp",EDGE,"E14.sketch_text.stroke-207"),sQuery(id+"F0.wireOp",EDGE,"E14.sketch_text.stroke-208"),sQuery(id+"F0.wireOp",EDGE,"E14.sketch_text.stroke-209"),sQuery(id+"F0.wireOp",EDGE,"E14.sketch_text.stroke-210")])]});
            var Q16;
            Q16=makeQuery(id+"F1.opExtrude","SWEPT_BODY",BODY,{"disambiguationData":[OSD([sQuery(id+"F0.wireOp",EDGE,"E14.sketch_text.stroke-211"),sQuery(id+"F0.wireOp",EDGE,"E14.sketch_text.stroke-212"),sQuery(id+"F0.wireOp",EDGE,"E14.sketch_text.stroke-213"),sQuery(id+"F0.wireOp",EDGE,"E14.sketch_text.stroke-214"),sQuery(id+"F0.wireOp",EDGE,"E14.sketch_text.stroke-215"),sQuery(id+"F0.wireOp",EDGE,"E14.sketch_text.stroke-216"),sQuery(id+"F0.wireOp",EDGE,"E14.sketch_text.stroke-217"),sQuery(id+"F0.wireOp",EDGE,"E14.sketch_text.stroke-218"),sQuery(id+"F0.wireOp",EDGE,"E14.sketch_text.stroke-219"),sQuery(id+"F0.wireOp",EDGE,"E14.sketch_text.stroke-220"),sQuery(id+"F0.wireOp",EDGE,"E14.sketch_text.stroke-221"),sQuery(id+"F0.wireOp",EDGE,"E14.sketch_text.stroke-222"),sQuery(id+"F0.wireOp",EDGE,"E14.sketch_text.stroke-223"),sQuery(id+"F0.wireOp",EDGE,"E14.sketch_text.stroke-224"),sQuery(id+"F0.wireOp",EDGE,"E14.sketch_text.stroke-225"),sQuery(id+"F0.wireOp",EDGE,"E14.sketch_text.stroke-226"),sQuery(id+"F0.wireOp",EDGE,"E14.sketch_text.stroke-227"),sQuery(id+"F0.wireOp",EDGE,"E14.sketch_text.stroke-228"),sQuery(id+"F0.wireOp",EDGE,"E14.sketch_text.stroke-229")])]});
            var Q17;
            Q17=makeQuery(id+"F1.opExtrude","SWEPT_BODY",BODY,{"disambiguationData":[OSD([sQuery(id+"F0.wireOp",EDGE,"E14.sketch_text.stroke-230"),sQuery(id+"F0.wireOp",EDGE,"E14.sketch_text.stroke-231"),sQuery(id+"F0.wireOp",EDGE,"E14.sketch_text.stroke-232"),sQuery(id+"F0.wireOp",EDGE,"E14.sketch_text.stroke-233"),sQuery(id+"F0.wireOp",EDGE,"E14.sketch_text.stroke-234"),sQuery(id+"F0.wireOp",EDGE,"E14.sketch_text.stroke-235"),sQuery(id+"F0.wireOp",EDGE,"E14.sketch_text.stroke-236"),sQuery(id+"F0.wireOp",EDGE,"E14.sketch_text.stroke-237"),sQuery(id+"F0.wireOp",EDGE,"E14.sketch_text.stroke-238"),sQuery(id+"F0.wireOp",EDGE,"E14.sketch_text.stroke-239"),sQuery(id+"F0.wireOp",EDGE,"E14.sketch_text.stroke-240"),sQuery(id+"F0.wireOp",EDGE,"E14.sketch_text.stroke-241"),sQuery(id+"F0.wireOp",EDGE,"E14.sketch_text.stroke-242"),sQuery(id+"F0.wireOp",EDGE,"E14.sketch_text.stroke-243"),sQuery(id+"F0.wireOp",EDGE,"E14.sketch_text.stroke-244"),sQuery(id+"F0.wireOp",EDGE,"E14.sketch_text.stroke-245"),sQuery(id+"F0.wireOp",EDGE,"E14.sketch_text.stroke-246")])]});
            var Q18;
            Q18=makeQuery(id+"F1.opExtrude","SWEPT_BODY",BODY,{"disambiguationData":[OSD([sQuery(id+"F0.wireOp",EDGE,"E14.sketch_text.stroke-247"),sQuery(id+"F0.wireOp",EDGE,"E14.sketch_text.stroke-248"),sQuery(id+"F0.wireOp",EDGE,"E14.sketch_text.stroke-249"),sQuery(id+"F0.wireOp",EDGE,"E14.sketch_text.stroke-250"),sQuery(id+"F0.wireOp",EDGE,"E14.sketch_text.stroke-251"),sQuery(id+"F0.wireOp",EDGE,"E14.sketch_text.stroke-252"),sQuery(id+"F0.wireOp",EDGE,"E14.sketch_text.stroke-253"),sQuery(id+"F0.wireOp",EDGE,"E14.sketch_text.stroke-254"),sQuery(id+"F0.wireOp",EDGE,"E14.sketch_text.stroke-255"),sQuery(id+"F0.wireOp",EDGE,"E14.sketch_text.stroke-256"),sQuery(id+"F0.wireOp",EDGE,"E14.sketch_text.stroke-257"),sQuery(id+"F0.wireOp",EDGE,"E14.sketch_text.stroke-258"),sQuery(id+"F0.wireOp",EDGE,"E14.sketch_text.stroke-259")])]});
            var Q19;
            Q19=makeQuery(id+"F1.opExtrude","SWEPT_BODY",BODY,{"disambiguationData":[OSD([sQuery(id+"F0.wireOp",EDGE,"E14.sketch_text.stroke-260"),sQuery(id+"F0.wireOp",EDGE,"E14.sketch_text.stroke-261"),sQuery(id+"F0.wireOp",EDGE,"E14.sketch_text.stroke-262"),sQuery(id+"F0.wireOp",EDGE,"E14.sketch_text.stroke-263"),sQuery(id+"F0.wireOp",EDGE,"E14.sketch_text.stroke-264"),sQuery(id+"F0.wireOp",EDGE,"E14.sketch_text.stroke-265"),sQuery(id+"F0.wireOp",EDGE,"E14.sketch_text.stroke-266"),sQuery(id+"F0.wireOp",EDGE,"E14.sketch_text.stroke-267"),sQuery(id+"F0.wireOp",EDGE,"E14.sketch_text.stroke-268"),sQuery(id+"F0.wireOp",EDGE,"E14.sketch_text.stroke-269"),sQuery(id+"F0.wireOp",EDGE,"E14.sketch_text.stroke-270"),sQuery(id+"F0.wireOp",EDGE,"E14.sketch_text.stroke-271"),sQuery(id+"F0.wireOp",EDGE,"E14.sketch_text.stroke-272"),sQuery(id+"F0.wireOp",EDGE,"E14.sketch_text.stroke-273"),sQuery(id+"F0.wireOp",EDGE,"E14.sketch_text.stroke-274"),sQuery(id+"F0.wireOp",EDGE,"E14.sketch_text.stroke-275"),sQuery(id+"F0.wireOp",EDGE,"E14.sketch_text.stroke-276"),sQuery(id+"F0.wireOp",EDGE,"E14.sketch_text.stroke-277"),sQuery(id+"F0.wireOp",EDGE,"E14.sketch_text.stroke-278")])]});
            var Q20;
            Q20=makeQuery(id+"F1.opExtrude","SWEPT_BODY",BODY,{"disambiguationData":[OSD([sQuery(id+"F0.wireOp",EDGE,"E14.sketch_text.stroke-279"),sQuery(id+"F0.wireOp",EDGE,"E14.sketch_text.stroke-280"),sQuery(id+"F0.wireOp",EDGE,"E14.sketch_text.stroke-281"),sQuery(id+"F0.wireOp",EDGE,"E14.sketch_text.stroke-282"),sQuery(id+"F0.wireOp",EDGE,"E14.sketch_text.stroke-283"),sQuery(id+"F0.wireOp",EDGE,"E14.sketch_text.stroke-284"),sQuery(id+"F0.wireOp",EDGE,"E14.sketch_text.stroke-285"),sQuery(id+"F0.wireOp",EDGE,"E14.sketch_text.stroke-286"),sQuery(id+"F0.wireOp",EDGE,"E14.sketch_text.stroke-287"),sQuery(id+"F0.wireOp",EDGE,"E14.sketch_text.stroke-288"),sQuery(id+"F0.wireOp",EDGE,"E14.sketch_text.stroke-289"),sQuery(id+"F0.wireOp",EDGE,"E14.sketch_text.stroke-290"),sQuery(id+"F0.wireOp",EDGE,"E14.sketch_text.stroke-291"),sQuery(id+"F0.wireOp",EDGE,"E14.sketch_text.stroke-292"),sQuery(id+"F0.wireOp",EDGE,"E14.sketch_text.stroke-293"),sQuery(id+"F0.wireOp",EDGE,"E14.sketch_text.stroke-294"),sQuery(id+"F0.wireOp",EDGE,"E14.sketch_text.stroke-295"),sQuery(id+"F0.wireOp",EDGE,"E14.sketch_text.stroke-296"),sQuery(id+"F0.wireOp",EDGE,"E14.sketch_text.stroke-297"),sQuery(id+"F0.wireOp",EDGE,"E14.sketch_text.stroke-298"),sQuery(id+"F0.wireOp",EDGE,"E14.sketch_text.stroke-299"),sQuery(id+"F0.wireOp",EDGE,"E14.sketch_text.stroke-300"),sQuery(id+"F0.wireOp",EDGE,"E14.sketch_text.stroke-301"),sQuery(id+"F0.wireOp",EDGE,"E14.sketch_text.stroke-302"),sQuery(id+"F0.wireOp",EDGE,"E14.sketch_text.stroke-303")])]});
            var Q21;
            Q21=makeQuery(id+"F1.opExtrude","SWEPT_BODY",BODY,{"disambiguationData":[OSD([sQuery(id+"F0.wireOp",EDGE,"E15.sketch_text.stroke-0"),sQuery(id+"F0.wireOp",EDGE,"E15.sketch_text.stroke-1"),sQuery(id+"F0.wireOp",EDGE,"E15.sketch_text.stroke-2"),sQuery(id+"F0.wireOp",EDGE,"E15.sketch_text.stroke-3"),sQuery(id+"F0.wireOp",EDGE,"E15.sketch_text.stroke-4"),sQuery(id+"F0.wireOp",EDGE,"E15.sketch_text.stroke-5"),sQuery(id+"F0.wireOp",EDGE,"E15.sketch_text.stroke-6"),sQuery(id+"F0.wireOp",EDGE,"E15.sketch_text.stroke-7"),sQuery(id+"F0.wireOp",EDGE,"E15.sketch_text.stroke-8"),sQuery(id+"F0.wireOp",EDGE,"E15.sketch_text.stroke-9"),sQuery(id+"F0.wireOp",EDGE,"E15.sketch_text.stroke-10"),sQuery(id+"F0.wireOp",EDGE,"E15.sketch_text.stroke-11"),sQuery(id+"F0.wireOp",EDGE,"E15.sketch_text.stroke-12"),sQuery(id+"F0.wireOp",EDGE,"E15.sketch_text.stroke-13"),sQuery(id+"F0.wireOp",EDGE,"E15.sketch_text.stroke-14")])]});
            var Q22;
            Q22=makeQuery(id+"F1.opExtrude","SWEPT_BODY",BODY,{"disambiguationData":[OSD([sQuery(id+"F0.wireOp",EDGE,"E15.sketch_text.stroke-15"),sQuery(id+"F0.wireOp",EDGE,"E15.sketch_text.stroke-16"),sQuery(id+"F0.wireOp",EDGE,"E15.sketch_text.stroke-17"),sQuery(id+"F0.wireOp",EDGE,"E15.sketch_text.stroke-18"),sQuery(id+"F0.wireOp",EDGE,"E15.sketch_text.stroke-19"),sQuery(id+"F0.wireOp",EDGE,"E15.sketch_text.stroke-20"),sQuery(id+"F0.wireOp",EDGE,"E15.sketch_text.stroke-21"),sQuery(id+"F0.wireOp",EDGE,"E15.sketch_text.stroke-22"),sQuery(id+"F0.wireOp",EDGE,"E15.sketch_text.stroke-23"),sQuery(id+"F0.wireOp",EDGE,"E15.sketch_text.stroke-24"),sQuery(id+"F0.wireOp",EDGE,"E15.sketch_text.stroke-25"),sQuery(id+"F0.wireOp",EDGE,"E15.sketch_text.stroke-26"),sQuery(id+"F0.wireOp",EDGE,"E15.sketch_text.stroke-27"),sQuery(id+"F0.wireOp",EDGE,"E15.sketch_text.stroke-28"),sQuery(id+"F0.wireOp",EDGE,"E15.sketch_text.stroke-29")])]});
            var Q23;
            Q23=makeQuery(id+"F1.opExtrude","SWEPT_BODY",BODY,{"disambiguationData":[OSD([sQuery(id+"F0.wireOp",EDGE,"E15.sketch_text.stroke-30"),sQuery(id+"F0.wireOp",EDGE,"E15.sketch_text.stroke-31"),sQuery(id+"F0.wireOp",EDGE,"E15.sketch_text.stroke-32"),sQuery(id+"F0.wireOp",EDGE,"E15.sketch_text.stroke-33")])]});
            var Q24;
            Q24=makeQuery(id+"F1.opExtrude","SWEPT_BODY",BODY,{"disambiguationData":[OSD([sQuery(id+"F0.wireOp",EDGE,"E15.sketch_text.stroke-34"),sQuery(id+"F0.wireOp",EDGE,"E15.sketch_text.stroke-35"),sQuery(id+"F0.wireOp",EDGE,"E15.sketch_text.stroke-36"),sQuery(id+"F0.wireOp",EDGE,"E15.sketch_text.stroke-37"),sQuery(id+"F0.wireOp",EDGE,"E15.sketch_text.stroke-38"),sQuery(id+"F0.wireOp",EDGE,"E15.sketch_text.stroke-39"),sQuery(id+"F0.wireOp",EDGE,"E15.sketch_text.stroke-40"),sQuery(id+"F0.wireOp",EDGE,"E15.sketch_text.stroke-41"),sQuery(id+"F0.wireOp",EDGE,"E15.sketch_text.stroke-42"),sQuery(id+"F0.wireOp",EDGE,"E15.sketch_text.stroke-43"),sQuery(id+"F0.wireOp",EDGE,"E15.sketch_text.stroke-44"),sQuery(id+"F0.wireOp",EDGE,"E15.sketch_text.stroke-45"),sQuery(id+"F0.wireOp",EDGE,"E15.sketch_text.stroke-46"),sQuery(id+"F0.wireOp",EDGE,"E15.sketch_text.stroke-47"),sQuery(id+"F0.wireOp",EDGE,"E15.sketch_text.stroke-48")])]});
            var Q25;
            Q25=makeQuery(id+"F1.opExtrude","SWEPT_BODY",BODY,{"disambiguationData":[OSD([sQuery(id+"F0.wireOp",EDGE,"E15.sketch_text.stroke-49"),sQuery(id+"F0.wireOp",EDGE,"E15.sketch_text.stroke-50"),sQuery(id+"F0.wireOp",EDGE,"E15.sketch_text.stroke-51"),sQuery(id+"F0.wireOp",EDGE,"E15.sketch_text.stroke-52"),sQuery(id+"F0.wireOp",EDGE,"E15.sketch_text.stroke-53"),sQuery(id+"F0.wireOp",EDGE,"E15.sketch_text.stroke-54"),sQuery(id+"F0.wireOp",EDGE,"E15.sketch_text.stroke-55"),sQuery(id+"F0.wireOp",EDGE,"E15.sketch_text.stroke-56"),sQuery(id+"F0.wireOp",EDGE,"E15.sketch_text.stroke-57"),sQuery(id+"F0.wireOp",EDGE,"E15.sketch_text.stroke-58"),sQuery(id+"F0.wireOp",EDGE,"E15.sketch_text.stroke-59"),sQuery(id+"F0.wireOp",EDGE,"E15.sketch_text.stroke-60"),sQuery(id+"F0.wireOp",EDGE,"E15.sketch_text.stroke-61"),sQuery(id+"F0.wireOp",EDGE,"E15.sketch_text.stroke-62"),sQuery(id+"F0.wireOp",EDGE,"E15.sketch_text.stroke-63"),sQuery(id+"F0.wireOp",EDGE,"E15.sketch_text.stroke-64")])]});
            var Q26;
            Q26=makeQuery(id+"F1.opExtrude","SWEPT_BODY",BODY,{"disambiguationData":[OSD([sQuery(id+"F0.wireOp",EDGE,"E15.sketch_text.stroke-65"),sQuery(id+"F0.wireOp",EDGE,"E15.sketch_text.stroke-66"),sQuery(id+"F0.wireOp",EDGE,"E15.sketch_text.stroke-67"),sQuery(id+"F0.wireOp",EDGE,"E15.sketch_text.stroke-68"),sQuery(id+"F0.wireOp",EDGE,"E15.sketch_text.stroke-69"),sQuery(id+"F0.wireOp",EDGE,"E15.sketch_text.stroke-70"),sQuery(id+"F0.wireOp",EDGE,"E15.sketch_text.stroke-71"),sQuery(id+"F0.wireOp",EDGE,"E15.sketch_text.stroke-72"),sQuery(id+"F0.wireOp",EDGE,"E15.sketch_text.stroke-73"),sQuery(id+"F0.wireOp",EDGE,"E15.sketch_text.stroke-74"),sQuery(id+"F0.wireOp",EDGE,"E15.sketch_text.stroke-75"),sQuery(id+"F0.wireOp",EDGE,"E15.sketch_text.stroke-76"),sQuery(id+"F0.wireOp",EDGE,"E15.sketch_text.stroke-77"),sQuery(id+"F0.wireOp",EDGE,"E15.sketch_text.stroke-78"),sQuery(id+"F0.wireOp",EDGE,"E15.sketch_text.stroke-79"),sQuery(id+"F0.wireOp",EDGE,"E15.sketch_text.stroke-80"),sQuery(id+"F0.wireOp",EDGE,"E15.sketch_text.stroke-81"),sQuery(id+"F0.wireOp",EDGE,"E15.sketch_text.stroke-82")])]});
            var Q27;
            Q27=makeQuery(id+"F1.opExtrude","SWEPT_BODY",BODY,{"disambiguationData":[OSD([sQuery(id+"F0.wireOp",EDGE,"E15.sketch_text.stroke-83"),sQuery(id+"F0.wireOp",EDGE,"E15.sketch_text.stroke-84"),sQuery(id+"F0.wireOp",EDGE,"E15.sketch_text.stroke-85"),sQuery(id+"F0.wireOp",EDGE,"E15.sketch_text.stroke-86"),sQuery(id+"F0.wireOp",EDGE,"E15.sketch_text.stroke-87"),sQuery(id+"F0.wireOp",EDGE,"E15.sketch_text.stroke-88"),sQuery(id+"F0.wireOp",EDGE,"E15.sketch_text.stroke-89"),sQuery(id+"F0.wireOp",EDGE,"E15.sketch_text.stroke-90")])]});
            var Q28;
            Q28=makeQuery(id+"F1.opExtrude","SWEPT_BODY",BODY,{"disambiguationData":[OSD([sQuery(id+"F0.wireOp",EDGE,"E15.sketch_text.stroke-91"),sQuery(id+"F0.wireOp",EDGE,"E15.sketch_text.stroke-92"),sQuery(id+"F0.wireOp",EDGE,"E15.sketch_text.stroke-93"),sQuery(id+"F0.wireOp",EDGE,"E15.sketch_text.stroke-94"),sQuery(id+"F0.wireOp",EDGE,"E15.sketch_text.stroke-95"),sQuery(id+"F0.wireOp",EDGE,"E15.sketch_text.stroke-96"),sQuery(id+"F0.wireOp",EDGE,"E15.sketch_text.stroke-97"),sQuery(id+"F0.wireOp",EDGE,"E15.sketch_text.stroke-98"),sQuery(id+"F0.wireOp",EDGE,"E15.sketch_text.stroke-99"),sQuery(id+"F0.wireOp",EDGE,"E15.sketch_text.stroke-100"),sQuery(id+"F0.wireOp",EDGE,"E15.sketch_text.stroke-101"),sQuery(id+"F0.wireOp",EDGE,"E15.sketch_text.stroke-102")])]});
            var Q29;
            Q29=makeQuery(id+"F1.opExtrude","SWEPT_BODY",BODY,{"disambiguationData":[OSD([sQuery(id+"F0.wireOp",EDGE,"E15.sketch_text.stroke-103"),sQuery(id+"F0.wireOp",EDGE,"E15.sketch_text.stroke-104"),sQuery(id+"F0.wireOp",EDGE,"E15.sketch_text.stroke-105"),sQuery(id+"F0.wireOp",EDGE,"E15.sketch_text.stroke-106"),sQuery(id+"F0.wireOp",EDGE,"E15.sketch_text.stroke-107"),sQuery(id+"F0.wireOp",EDGE,"E15.sketch_text.stroke-108"),sQuery(id+"F0.wireOp",EDGE,"E15.sketch_text.stroke-109"),sQuery(id+"F0.wireOp",EDGE,"E15.sketch_text.stroke-110"),sQuery(id+"F0.wireOp",EDGE,"E15.sketch_text.stroke-111"),sQuery(id+"F0.wireOp",EDGE,"E15.sketch_text.stroke-112"),sQuery(id+"F0.wireOp",EDGE,"E15.sketch_text.stroke-113"),sQuery(id+"F0.wireOp",EDGE,"E15.sketch_text.stroke-114"),sQuery(id+"F0.wireOp",EDGE,"E15.sketch_text.stroke-115"),sQuery(id+"F0.wireOp",EDGE,"E15.sketch_text.stroke-116"),sQuery(id+"F0.wireOp",EDGE,"E15.sketch_text.stroke-117"),sQuery(id+"F0.wireOp",EDGE,"E15.sketch_text.stroke-118"),sQuery(id+"F0.wireOp",EDGE,"E15.sketch_text.stroke-119"),sQuery(id+"F0.wireOp",EDGE,"E15.sketch_text.stroke-120"),sQuery(id+"F0.wireOp",EDGE,"E15.sketch_text.stroke-121"),sQuery(id+"F0.wireOp",EDGE,"E15.sketch_text.stroke-122"),sQuery(id+"F0.wireOp",EDGE,"E15.sketch_text.stroke-123"),sQuery(id+"F0.wireOp",EDGE,"E15.sketch_text.stroke-124"),sQuery(id+"F0.wireOp",EDGE,"E15.sketch_text.stroke-125"),sQuery(id+"F0.wireOp",EDGE,"E15.sketch_text.stroke-126"),sQuery(id+"F0.wireOp",EDGE,"E15.sketch_text.stroke-127")])]});
            var Q30;
            Q30=makeQuery(id+"F1.opExtrude","SWEPT_BODY",BODY,{"disambiguationData":[OSD([sQuery(id+"F0.wireOp",EDGE,"E15.sketch_text.stroke-128"),sQuery(id+"F0.wireOp",EDGE,"E15.sketch_text.stroke-129"),sQuery(id+"F0.wireOp",EDGE,"E15.sketch_text.stroke-130"),sQuery(id+"F0.wireOp",EDGE,"E15.sketch_text.stroke-131"),sQuery(id+"F0.wireOp",EDGE,"E15.sketch_text.stroke-132"),sQuery(id+"F0.wireOp",EDGE,"E15.sketch_text.stroke-133"),sQuery(id+"F0.wireOp",EDGE,"E15.sketch_text.stroke-134"),sQuery(id+"F0.wireOp",EDGE,"E15.sketch_text.stroke-135"),sQuery(id+"F0.wireOp",EDGE,"E15.sketch_text.stroke-136"),sQuery(id+"F0.wireOp",EDGE,"E15.sketch_text.stroke-137"),sQuery(id+"F0.wireOp",EDGE,"E15.sketch_text.stroke-138"),sQuery(id+"F0.wireOp",EDGE,"E15.sketch_text.stroke-139"),sQuery(id+"F0.wireOp",EDGE,"E15.sketch_text.stroke-140"),sQuery(id+"F0.wireOp",EDGE,"E15.sketch_text.stroke-141")])]});
            var Q31;
            Q31=makeQuery(id+"F1.opExtrude","SWEPT_BODY",BODY,{"disambiguationData":[OSD([sQuery(id+"F0.wireOp",EDGE,"E15.sketch_text.stroke-142"),sQuery(id+"F0.wireOp",EDGE,"E15.sketch_text.stroke-143"),sQuery(id+"F0.wireOp",EDGE,"E15.sketch_text.stroke-144"),sQuery(id+"F0.wireOp",EDGE,"E15.sketch_text.stroke-145"),sQuery(id+"F0.wireOp",EDGE,"E15.sketch_text.stroke-146"),sQuery(id+"F0.wireOp",EDGE,"E15.sketch_text.stroke-147"),sQuery(id+"F0.wireOp",EDGE,"E15.sketch_text.stroke-148"),sQuery(id+"F0.wireOp",EDGE,"E15.sketch_text.stroke-149"),sQuery(id+"F0.wireOp",EDGE,"E15.sketch_text.stroke-150"),sQuery(id+"F0.wireOp",EDGE,"E15.sketch_text.stroke-151"),sQuery(id+"F0.wireOp",EDGE,"E15.sketch_text.stroke-152"),sQuery(id+"F0.wireOp",EDGE,"E15.sketch_text.stroke-153")])]});
            var Q32;
            Q32=makeQuery(id+"F1.opExtrude","SWEPT_BODY",BODY,{"disambiguationData":[OSD([sQuery(id+"F0.wireOp",EDGE,"E15.sketch_text.stroke-154"),sQuery(id+"F0.wireOp",EDGE,"E15.sketch_text.stroke-155"),sQuery(id+"F0.wireOp",EDGE,"E15.sketch_text.stroke-156"),sQuery(id+"F0.wireOp",EDGE,"E15.sketch_text.stroke-157"),sQuery(id+"F0.wireOp",EDGE,"E15.sketch_text.stroke-158"),sQuery(id+"F0.wireOp",EDGE,"E15.sketch_text.stroke-159"),sQuery(id+"F0.wireOp",EDGE,"E15.sketch_text.stroke-160"),sQuery(id+"F0.wireOp",EDGE,"E15.sketch_text.stroke-161"),sQuery(id+"F0.wireOp",EDGE,"E15.sketch_text.stroke-162"),sQuery(id+"F0.wireOp",EDGE,"E15.sketch_text.stroke-163"),sQuery(id+"F0.wireOp",EDGE,"E15.sketch_text.stroke-164"),sQuery(id+"F0.wireOp",EDGE,"E15.sketch_text.stroke-165"),sQuery(id+"F0.wireOp",EDGE,"E15.sketch_text.stroke-166"),sQuery(id+"F0.wireOp",EDGE,"E15.sketch_text.stroke-167"),sQuery(id+"F0.wireOp",EDGE,"E15.sketch_text.stroke-168")])]});
            var Q33;
            Q33=makeQuery(id+"F1.opExtrude","SWEPT_BODY",BODY,{"disambiguationData":[OSD([sQuery(id+"F0.wireOp",EDGE,"E15.sketch_text.stroke-169"),sQuery(id+"F0.wireOp",EDGE,"E15.sketch_text.stroke-170"),sQuery(id+"F0.wireOp",EDGE,"E15.sketch_text.stroke-171"),sQuery(id+"F0.wireOp",EDGE,"E15.sketch_text.stroke-172"),sQuery(id+"F0.wireOp",EDGE,"E15.sketch_text.stroke-173"),sQuery(id+"F0.wireOp",EDGE,"E15.sketch_text.stroke-174"),sQuery(id+"F0.wireOp",EDGE,"E15.sketch_text.stroke-175"),sQuery(id+"F0.wireOp",EDGE,"E15.sketch_text.stroke-176"),sQuery(id+"F0.wireOp",EDGE,"E15.sketch_text.stroke-177"),sQuery(id+"F0.wireOp",EDGE,"E15.sketch_text.stroke-178"),sQuery(id+"F0.wireOp",EDGE,"E15.sketch_text.stroke-179"),sQuery(id+"F0.wireOp",EDGE,"E15.sketch_text.stroke-180"),sQuery(id+"F0.wireOp",EDGE,"E15.sketch_text.stroke-181"),sQuery(id+"F0.wireOp",EDGE,"E15.sketch_text.stroke-182"),sQuery(id+"F0.wireOp",EDGE,"E15.sketch_text.stroke-183"),sQuery(id+"F0.wireOp",EDGE,"E15.sketch_text.stroke-184")])]});
            var Q34;
            Q34=makeQuery(id+"F1.opExtrude","SWEPT_BODY",BODY,{"disambiguationData":[OSD([sQuery(id+"F0.wireOp",EDGE,"E15.sketch_text.stroke-185"),sQuery(id+"F0.wireOp",EDGE,"E15.sketch_text.stroke-186"),sQuery(id+"F0.wireOp",EDGE,"E15.sketch_text.stroke-187"),sQuery(id+"F0.wireOp",EDGE,"E15.sketch_text.stroke-188"),sQuery(id+"F0.wireOp",EDGE,"E15.sketch_text.stroke-189"),sQuery(id+"F0.wireOp",EDGE,"E15.sketch_text.stroke-190"),sQuery(id+"F0.wireOp",EDGE,"E15.sketch_text.stroke-191"),sQuery(id+"F0.wireOp",EDGE,"E15.sketch_text.stroke-192"),sQuery(id+"F0.wireOp",EDGE,"E15.sketch_text.stroke-193"),sQuery(id+"F0.wireOp",EDGE,"E15.sketch_text.stroke-194"),sQuery(id+"F0.wireOp",EDGE,"E15.sketch_text.stroke-195"),sQuery(id+"F0.wireOp",EDGE,"E15.sketch_text.stroke-196"),sQuery(id+"F0.wireOp",EDGE,"E15.sketch_text.stroke-197"),sQuery(id+"F0.wireOp",EDGE,"E15.sketch_text.stroke-198"),sQuery(id+"F0.wireOp",EDGE,"E15.sketch_text.stroke-199"),sQuery(id+"F0.wireOp",EDGE,"E15.sketch_text.stroke-200"),sQuery(id+"F0.wireOp",EDGE,"E15.sketch_text.stroke-201"),sQuery(id+"F0.wireOp",EDGE,"E15.sketch_text.stroke-202")])]});
            var Q35;
            Q35=makeQuery(id+"F1.opExtrude","SWEPT_BODY",BODY,{"disambiguationData":[OSD([sQuery(id+"F0.wireOp",EDGE,"E15.sketch_text.stroke-203"),sQuery(id+"F0.wireOp",EDGE,"E15.sketch_text.stroke-204"),sQuery(id+"F0.wireOp",EDGE,"E15.sketch_text.stroke-205"),sQuery(id+"F0.wireOp",EDGE,"E15.sketch_text.stroke-206"),sQuery(id+"F0.wireOp",EDGE,"E15.sketch_text.stroke-207"),sQuery(id+"F0.wireOp",EDGE,"E15.sketch_text.stroke-208"),sQuery(id+"F0.wireOp",EDGE,"E15.sketch_text.stroke-209"),sQuery(id+"F0.wireOp",EDGE,"E15.sketch_text.stroke-210"),sQuery(id+"F0.wireOp",EDGE,"E15.sketch_text.stroke-211"),sQuery(id+"F0.wireOp",EDGE,"E15.sketch_text.stroke-212"),sQuery(id+"F0.wireOp",EDGE,"E15.sketch_text.stroke-213"),sQuery(id+"F0.wireOp",EDGE,"E15.sketch_text.stroke-214"),sQuery(id+"F0.wireOp",EDGE,"E15.sketch_text.stroke-215"),sQuery(id+"F0.wireOp",EDGE,"E15.sketch_text.stroke-216"),sQuery(id+"F0.wireOp",EDGE,"E15.sketch_text.stroke-217"),sQuery(id+"F0.wireOp",EDGE,"E15.sketch_text.stroke-218"),sQuery(id+"F0.wireOp",EDGE,"E15.sketch_text.stroke-219"),sQuery(id+"F0.wireOp",EDGE,"E15.sketch_text.stroke-220")])]});
            var Q36;
            Q36=makeQuery(id+"F1.opExtrude","SWEPT_BODY",BODY,{"disambiguationData":[OSD([sQuery(id+"F0.wireOp",EDGE,"E15.sketch_text.stroke-221"),sQuery(id+"F0.wireOp",EDGE,"E15.sketch_text.stroke-222"),sQuery(id+"F0.wireOp",EDGE,"E15.sketch_text.stroke-223"),sQuery(id+"F0.wireOp",EDGE,"E15.sketch_text.stroke-224"),sQuery(id+"F0.wireOp",EDGE,"E15.sketch_text.stroke-225"),sQuery(id+"F0.wireOp",EDGE,"E15.sketch_text.stroke-226"),sQuery(id+"F0.wireOp",EDGE,"E15.sketch_text.stroke-227"),sQuery(id+"F0.wireOp",EDGE,"E15.sketch_text.stroke-228"),sQuery(id+"F0.wireOp",EDGE,"E15.sketch_text.stroke-229"),sQuery(id+"F0.wireOp",EDGE,"E15.sketch_text.stroke-230"),sQuery(id+"F0.wireOp",EDGE,"E15.sketch_text.stroke-231"),sQuery(id+"F0.wireOp",EDGE,"E15.sketch_text.stroke-232"),sQuery(id+"F0.wireOp",EDGE,"E15.sketch_text.stroke-233")])]});
            var Q37;
            Q37=makeQuery(id+"F1.opExtrude","SWEPT_BODY",BODY,{"disambiguationData":[OSD([sQuery(id+"F0.wireOp",EDGE,"E15.sketch_text.stroke-234"),sQuery(id+"F0.wireOp",EDGE,"E15.sketch_text.stroke-235"),sQuery(id+"F0.wireOp",EDGE,"E15.sketch_text.stroke-236"),sQuery(id+"F0.wireOp",EDGE,"E15.sketch_text.stroke-237"),sQuery(id+"F0.wireOp",EDGE,"E15.sketch_text.stroke-238"),sQuery(id+"F0.wireOp",EDGE,"E15.sketch_text.stroke-239"),sQuery(id+"F0.wireOp",EDGE,"E15.sketch_text.stroke-240"),sQuery(id+"F0.wireOp",EDGE,"E15.sketch_text.stroke-241"),sQuery(id+"F0.wireOp",EDGE,"E15.sketch_text.stroke-242"),sQuery(id+"F0.wireOp",EDGE,"E15.sketch_text.stroke-243"),sQuery(id+"F0.wireOp",EDGE,"E15.sketch_text.stroke-244"),sQuery(id+"F0.wireOp",EDGE,"E15.sketch_text.stroke-245"),sQuery(id+"F0.wireOp",EDGE,"E15.sketch_text.stroke-246"),sQuery(id+"F0.wireOp",EDGE,"E15.sketch_text.stroke-247"),sQuery(id+"F0.wireOp",EDGE,"E15.sketch_text.stroke-248")])]});
            var Q38;
            Q38=makeQuery(id+"F1.opExtrude","SWEPT_BODY",BODY,{"disambiguationData":[OSD([sQuery(id+"F0.wireOp",EDGE,"E15.sketch_text.stroke-249"),sQuery(id+"F0.wireOp",EDGE,"E15.sketch_text.stroke-250"),sQuery(id+"F0.wireOp",EDGE,"E15.sketch_text.stroke-251"),sQuery(id+"F0.wireOp",EDGE,"E15.sketch_text.stroke-252"),sQuery(id+"F0.wireOp",EDGE,"E15.sketch_text.stroke-253"),sQuery(id+"F0.wireOp",EDGE,"E15.sketch_text.stroke-254"),sQuery(id+"F0.wireOp",EDGE,"E15.sketch_text.stroke-255"),sQuery(id+"F0.wireOp",EDGE,"E15.sketch_text.stroke-256"),sQuery(id+"F0.wireOp",EDGE,"E15.sketch_text.stroke-257"),sQuery(id+"F0.wireOp",EDGE,"E15.sketch_text.stroke-258"),sQuery(id+"F0.wireOp",EDGE,"E15.sketch_text.stroke-259"),sQuery(id+"F0.wireOp",EDGE,"E15.sketch_text.stroke-260"),sQuery(id+"F0.wireOp",EDGE,"E15.sketch_text.stroke-261"),sQuery(id+"F0.wireOp",EDGE,"E15.sketch_text.stroke-262")])]});
            var Q39;
            Q39=makeQuery(id+"F1.opExtrude","SWEPT_BODY",BODY,{"disambiguationData":[OSD([sQuery(id+"F0.wireOp",EDGE,"E15.sketch_text.stroke-263"),sQuery(id+"F0.wireOp",EDGE,"E15.sketch_text.stroke-264"),sQuery(id+"F0.wireOp",EDGE,"E15.sketch_text.stroke-265"),sQuery(id+"F0.wireOp",EDGE,"E15.sketch_text.stroke-266")])]});
            var Q40;
            Q40=makeQuery(id+"F1.opExtrude","SWEPT_BODY",BODY,{"disambiguationData":[OSD([sQuery(id+"F0.wireOp",EDGE,"E15.sketch_text.stroke-267"),sQuery(id+"F0.wireOp",EDGE,"E15.sketch_text.stroke-268"),sQuery(id+"F0.wireOp",EDGE,"E15.sketch_text.stroke-269"),sQuery(id+"F0.wireOp",EDGE,"E15.sketch_text.stroke-270"),sQuery(id+"F0.wireOp",EDGE,"E15.sketch_text.stroke-271"),sQuery(id+"F0.wireOp",EDGE,"E15.sketch_text.stroke-272"),sQuery(id+"F0.wireOp",EDGE,"E15.sketch_text.stroke-273"),sQuery(id+"F0.wireOp",EDGE,"E15.sketch_text.stroke-274"),sQuery(id+"F0.wireOp",EDGE,"E15.sketch_text.stroke-275"),sQuery(id+"F0.wireOp",EDGE,"E15.sketch_text.stroke-276"),sQuery(id+"F0.wireOp",EDGE,"E15.sketch_text.stroke-277"),sQuery(id+"F0.wireOp",EDGE,"E15.sketch_text.stroke-278")])]});
            var Q41;
            Q41=makeQuery(id+"F3.opExtrude","SWEPT_BODY",BODY,{"disambiguationData":[OSD([sQuery(id+"F2.wireOp",EDGE,"E16.bottom"),sQuery(id+"F2.wireOp",EDGE,"E16.top"),sQuery(id+"F2.wireOp",EDGE,"E16.left"),sQuery(id+"F2.wireOp",EDGE,"E16.right")])]});
            deleteBodies(context, id + "F6", {"entities" : qUnion([Q0, Q1, Q2, Q3, Q4, Q5, Q6, Q7, Q8, Q9, Q10, Q11, Q12, Q13, Q14, Q15, Q16, Q17, Q18, Q19, Q20, Q21, Q22, Q23, Q24, Q25, Q26, Q27, Q28, Q29, Q30, Q31, Q32, Q33, Q34, Q35, Q36, Q37, Q38, Q39, Q40, Q41])});
        }
    });
